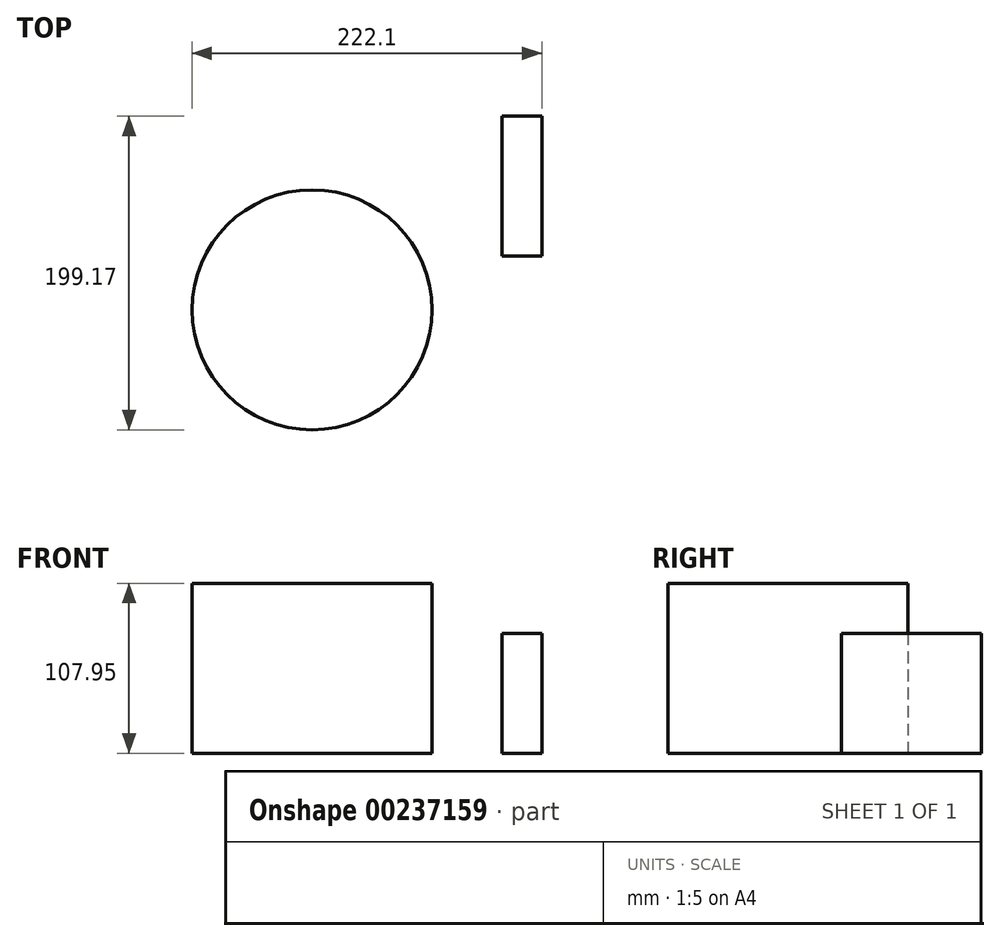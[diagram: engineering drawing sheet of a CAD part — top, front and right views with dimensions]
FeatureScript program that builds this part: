
annotation { "Feature Type Name" : "Feature", "Feature Type Description" : "" }
export const myFeature = defineFeature(function(context is Context, id is Id, definition is map)
    precondition{}
    {
        {
            var Q0;
            Q0=qCreatedBy(makeId("Top.planeOp"),FACE);
            var sketch = newSketch(context, id + "F0", { "sketchPlane" : qUnion([Q0])});
            skCircle(sketch, "E0", {"center": v(-41.92, -51.62) * mm, "radius": 76.2 * mm});
            skSolve(sketch);
        }
        {
            var Q0;
            Q0 = qSketchRegion(id + "F0", true);
            extrude(context, id + "F1", {"entities" : qUnion([Q0]), "depth" : 107.95 * mm});
        }
        {
            var Q0;
            Q0=qCreatedBy(makeId("Top.planeOp"),FACE);
            var sketch = newSketch(context, id + "F2", { "sketchPlane" : qUnion([Q0])});
            skLineSegment(sketch, "E1.bottom", {"start": v(103.98, -17.55) * mm, "end": v(78.58, -17.55) * mm});
            skLineSegment(sketch, "E1.top", {"start": v(103.98, 71.35) * mm, "end": v(78.58, 71.35) * mm});
            skLineSegment(sketch, "E1.left", {"start": v(103.98, -17.55) * mm, "end": v(103.98, 71.35) * mm});
            skLineSegment(sketch, "E1.right", {"start": v(78.58, -17.55) * mm, "end": v(78.58, 71.35) * mm});
            skSolve(sketch);
        }
        {
            var Q0;
            Q0 = qSketchRegion(id + "F2", true);
            extrude(context, id + "F3", {"entities" : qUnion([Q0]), "depth" : 76.2 * mm});
        }
    });
